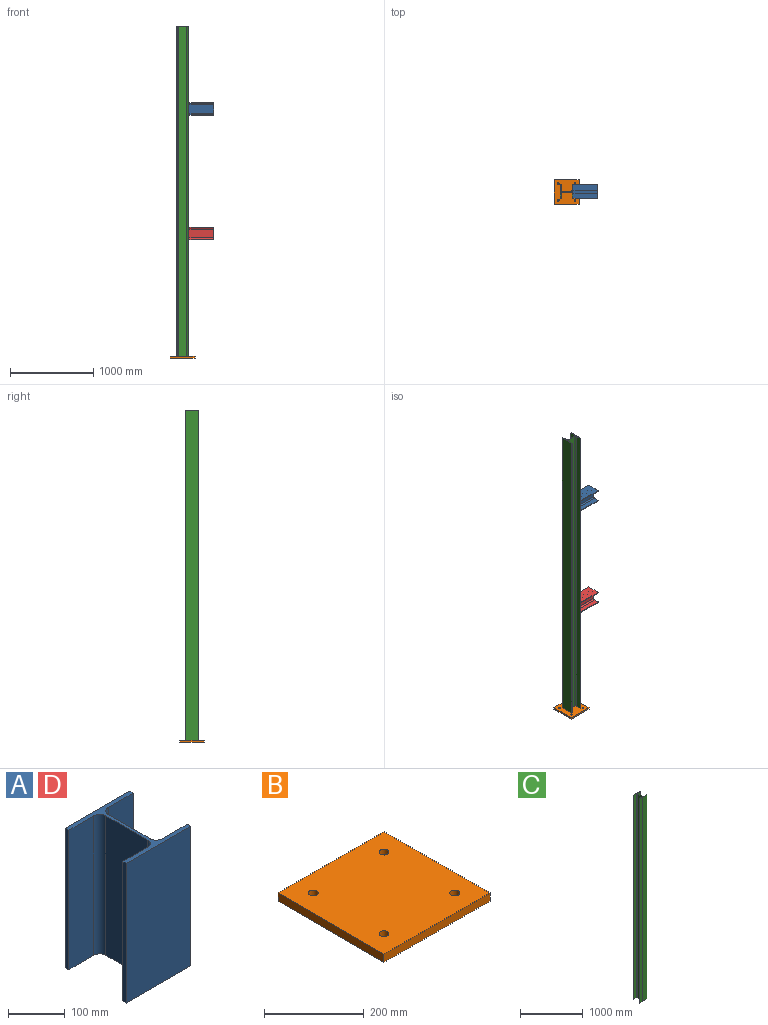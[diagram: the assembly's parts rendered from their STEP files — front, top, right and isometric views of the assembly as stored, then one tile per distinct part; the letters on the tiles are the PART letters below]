
ASSEMBLY  parts=4 mates=2
PART A: 18 faces, bbox 160x152x300 mm
  f0: plane 300x9mm, normal (-1,0,0), area 2700mm2, adj f1,f15,f16,f17
  f1: plane 300x62mm, normal (0,1,0), area 18600mm2, adj f0,f2,f16,f17
  f2: cylinder r=15mm len=300mm, axis (0,0,1), area 7068.6mm2, adj f1,f3,f16,f17
  f3: plane 300x104mm, normal (-1,0,0), area 31200mm2, adj f2,f4,f16,f17
  f4: cylinder r=15mm len=300mm, axis (0,0,1), area 7068.6mm2, adj f3,f5,f16,f17
  f5: plane 300x62mm, normal (0,-1,0), area 18600mm2, adj f4,f6,f16,f17
  f6: plane 300x9mm, normal (-1,0,0), area 2700mm2, adj f5,f7,f16,f17
  f7: plane 300x160mm, normal (0,1,0), area 48000mm2, adj f6,f8,f16,f17
  f8: plane 300x9mm, normal (1,0,0), area 2700mm2, adj f7,f9,f16,f17
  f9: plane 300x62mm, normal (0,-1,0), area 18600mm2, adj f8,f10,f16,f17
  f10: cylinder r=15mm len=300mm, axis (0,0,1), area 7068.6mm2, adj f9,f11,f16,f17
  f11: plane 300x104mm, normal (1,0,0), area 31200mm2, adj f10,f12,f16,f17
  f12: cylinder r=15mm len=300mm, axis (0,0,1), area 7068.6mm2, adj f11,f13,f16,f17
  f13: plane 300x62mm, normal (0,1,0), area 18600mm2, adj f12,f14,f16,f17
  f14: plane 300x9mm, normal (1,0,0), area 2700mm2, adj f13,f15,f16,f17
  f15: plane 300x160mm, normal (0,-1,0), area 48000mm2, adj f0,f14,f16,f17
  f16: plane 160x152mm, normal (0,0,1), area 3877.1mm2, adj f0,f1,f2,f3,f4,f5,f6,f7
  f17: plane 160x152mm, normal (0,0,-1), area 3877.1mm2, adj f0,f1,f2,f3,f4,f5,f6,f7
PART B: 10 faces, bbox 300x300x20 mm
  f0: plane 300x20mm, normal (1,0,0), area 6000mm2, adj f1,f6,f8,f9
  f1: plane 300x20mm, normal (0,1,0), area 6000mm2, adj f0,f2,f8,f9
  f2: plane 300x20mm, normal (-1,0,0), area 6000mm2, adj f1,f6,f8,f9
  f3: cylinder r=10mm len=20mm, axis (0,0,-1), area 1256.6mm2, adj f8,f9
  f4: cylinder r=10mm len=20mm, axis (0,0,-1), area 1256.6mm2, adj f8,f9
  f5: cylinder r=10mm len=20mm, axis (0,0,-1), area 1256.6mm2, adj f8,f9
  f6: plane 300x20mm, normal (0,-1,0), area 6000mm2, adj f0,f2,f8,f9
  f7: cylinder r=10mm len=20mm, axis (0,0,-1), area 1256.6mm2, adj f8,f9
  f8: plane 300x300mm, normal (0,0,1), area 88743.4mm2, adj f0,f1,f2,f3,f4,f5,f6,f7
  f9: plane 300x300mm, normal (0,0,-1), area 88743.4mm2, adj f0,f1,f2,f3,f4,f5,f6,f7
PART C: 18 faces, bbox 160x152x3980 mm
  f0: plane 3980x9mm, normal (-1,0,0), area 35820mm2, adj f1,f15,f16,f17
  f1: plane 3980x62mm, normal (0,1,0), area 246760mm2, adj f0,f2,f16,f17
  f2: cylinder r=15mm len=3980mm, axis (0,0,1), area 93776.5mm2, adj f1,f3,f16,f17
  f3: plane 3980x104mm, normal (-1,0,0), area 413920mm2, adj f2,f4,f16,f17
  f4: cylinder r=15mm len=3980mm, axis (0,0,1), area 93776.5mm2, adj f3,f5,f16,f17
  f5: plane 3980x62mm, normal (0,-1,0), area 246760mm2, adj f4,f6,f16,f17
  f6: plane 3980x9mm, normal (-1,0,0), area 35820mm2, adj f5,f7,f16,f17
  f7: plane 3980x160mm, normal (0,1,0), area 636800mm2, adj f6,f8,f16,f17
  f8: plane 3980x9mm, normal (1,0,0), area 35820mm2, adj f7,f9,f16,f17
  f9: plane 3980x62mm, normal (0,-1,0), area 246760mm2, adj f8,f10,f16,f17
  f10: cylinder r=15mm len=3980mm, axis (0,0,1), area 93776.5mm2, adj f9,f11,f16,f17
  f11: plane 3980x104mm, normal (1,0,0), area 413920mm2, adj f10,f12,f16,f17
  f12: cylinder r=15mm len=3980mm, axis (0,0,1), area 93776.5mm2, adj f11,f13,f16,f17
  f13: plane 3980x62mm, normal (0,1,0), area 246760mm2, adj f12,f14,f16,f17
  f14: plane 3980x9mm, normal (1,0,0), area 35820mm2, adj f13,f15,f16,f17
  f15: plane 3980x160mm, normal (0,-1,0), area 636800mm2, adj f0,f14,f16,f17
  f16: plane 160x152mm, normal (0,0,1), area 3877.1mm2, adj f0,f1,f2,f3,f4,f5,f6,f7
  f17: plane 160x152mm, normal (0,0,-1), area 3877.1mm2, adj f0,f1,f2,f3,f4,f5,f6,f7
PART D: same geometry as A
PLACE A rot(axis=(0.58,-0.58,-0.58),120deg) t=(226,0,3000)mm
PLACE B at identity
PLACE C rot(axis=(0,0,1),90deg) t=(0,0,2010)mm
PLACE D rot(axis=(0.58,-0.58,-0.58),120deg) t=(226,0,1500)mm
MATE fastened D.f16 <-> C.f15  axis (-1,0,0) through (76,0,1500)mm
MATE fastened C.f17 <-> B.f8  axis (0,0,-1) through (0,0,20)mm
